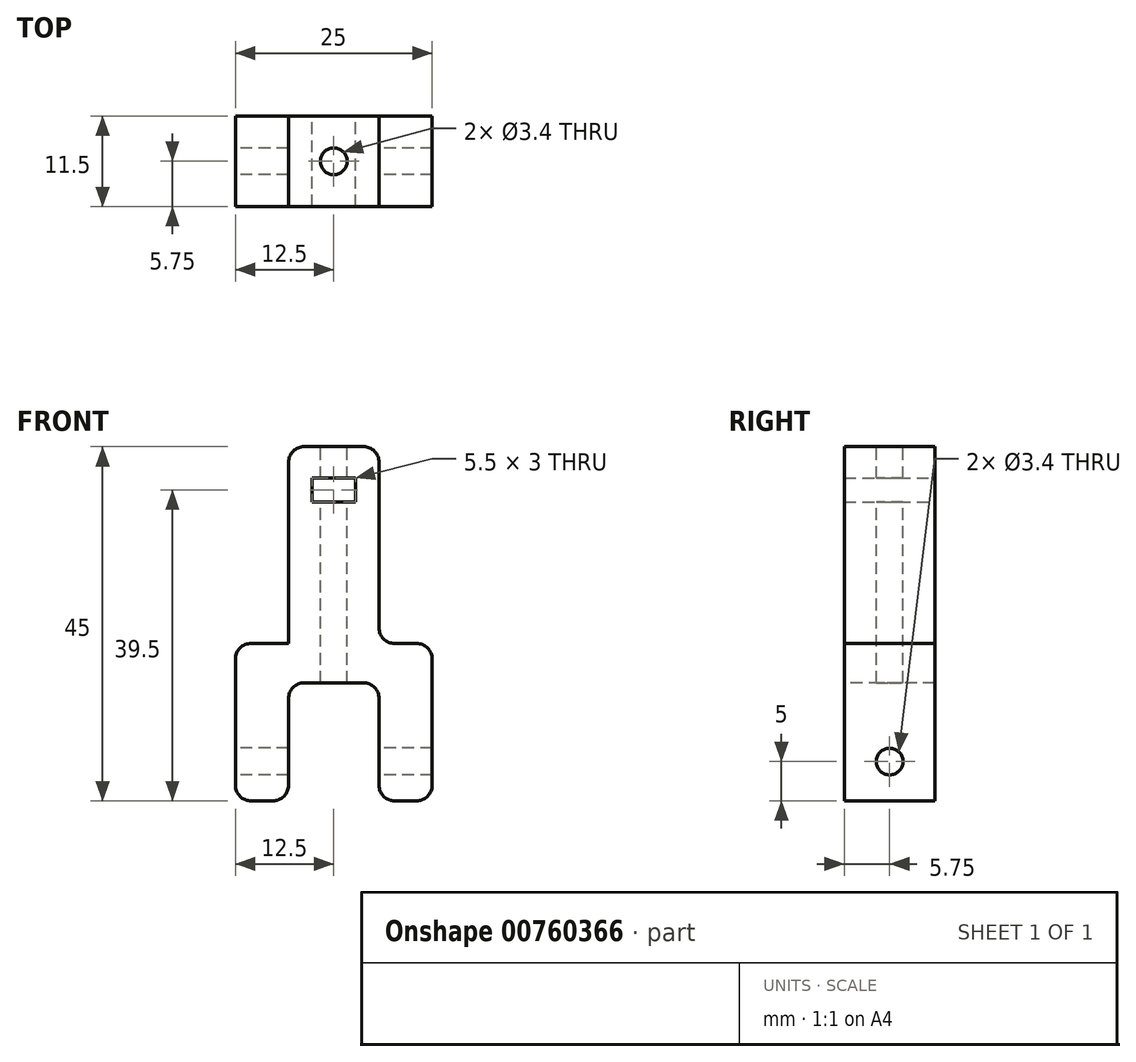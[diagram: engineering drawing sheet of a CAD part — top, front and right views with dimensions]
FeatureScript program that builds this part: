
annotation { "Feature Type Name" : "Feature", "Feature Type Description" : "" }
export const myFeature = defineFeature(function(context is Context, id is Id, definition is map)
    precondition{}
    {
        {
            var Q0;
            Q0=qCreatedBy(makeId("Top.planeOp"),FACE);
            var sketch = newSketch(context, id + "F0", { "sketchPlane" : qUnion([Q0])});
            skLineSegment(sketch, "E0.bottom", {"start": v(5.75, 5.75) * mm, "end": v(-5.75, 5.75) * mm});
            skLineSegment(sketch, "E0.top", {"start": v(5.75, -5.75) * mm, "end": v(-5.75, -5.75) * mm});
            skLineSegment(sketch, "E0.left", {"start": v(5.75, 5.75) * mm, "end": v(5.75, -5.75) * mm});
            skLineSegment(sketch, "E0.right", {"start": v(-5.75, 5.75) * mm, "end": v(-5.75, -5.75) * mm});
            skPoint(sketch, "E0.middle", {"position": v(0, 0) * mm});
            skLineSegment(sketch, "E1.bottom", {"start": v(12.5, 5.75) * mm, "end": v(-12.5, 5.75) * mm});
            skLineSegment(sketch, "E1.top", {"start": v(12.5, -5.75) * mm, "end": v(-12.5, -5.75) * mm});
            skLineSegment(sketch, "E1.left", {"start": v(12.5, 5.75) * mm, "end": v(12.5, -5.75) * mm});
            skLineSegment(sketch, "E1.right", {"start": v(-12.5, 5.75) * mm, "end": v(-12.5, -5.75) * mm});
            skSolve(sketch);
        }
        {
            var Q0;
            {var subQ0=sQuery(id+"F0.wireOp",EDGE,"E0.right");Q0=makeQuery(id+"F0.imprint","IMPRINT",FACE,{"disambiguationData":[TD([[makeQuery(id+"F0.imprint","IMPRINT",EDGE,{"derivedFrom":subQ0}),-1.0]])]});}
            var Q1;
            {var subQ0=sQuery(id+"F0.wireOp",EDGE,"E0.left");Q1=makeQuery(id+"F0.imprint","IMPRINT",FACE,{"disambiguationData":[TD([[makeQuery(id+"F0.imprint","IMPRINT",EDGE,{"derivedFrom":subQ0}),1.0]])]});}
            var Q2;
            {var subQ0=sQuery(id+"F0.wireOp",EDGE,"E0.left");Q2=makeQuery(id+"F0.imprint","IMPRINT",FACE,{"disambiguationData":[TD([[makeQuery(id+"F0.imprint","IMPRINT",EDGE,{"derivedFrom":subQ0}),-1.0]])]});}
            extrude(context, id + "F1", {"entities" : qUnion([Q0, Q1, Q2]), "oppositeDirection" : true, "depth" : 5 * mm});
        }
        {
            var Q0;
            {var subQ0=sQuery(id+"F0.wireOp",EDGE,"E0.left");Q0=makeQuery(id+"F0.imprint","IMPRINT",FACE,{"disambiguationData":[TD([[makeQuery(id+"F0.imprint","IMPRINT",EDGE,{"derivedFrom":subQ0}),1.0]])]});}
            var Q1;
            {var subQ0=sQuery(id+"F0.wireOp",EDGE,"E0.right");Q1=makeQuery(id+"F0.imprint","IMPRINT",FACE,{"disambiguationData":[TD([[makeQuery(id+"F0.imprint","IMPRINT",EDGE,{"derivedFrom":subQ0}),-1.0]])]});}
            extrude(context, id + "F2", {"entities" : qUnion([Q0, Q1]), "operationType" : NewBodyOperationType.ADD, "oppositeDirection" : true, "depth" : 20 * mm});
        }
        {
            var Q0;
            {var subQ0=sQuery(id+"F0.wireOp",EDGE,"E0.left");Q0=makeQuery(id+"F0.imprint","IMPRINT",FACE,{"disambiguationData":[TD([[makeQuery(id+"F0.imprint","IMPRINT",EDGE,{"derivedFrom":subQ0}),-1.0]])]});}
            extrude(context, id + "F3", {"entities" : qUnion([Q0]), "operationType" : NewBodyOperationType.ADD, "depth" : 25 * mm});
        }
        {
            var Q0;
            {var subQ0=sQuery(id+"F0.wireOp",EDGE,"E1.right");Q0=makeQuery(id+"F2.boolean.opBoolean","MERGE",FACE,{"derivedFrom":[makeQuery(id+"F1.opExtrude","SWEPT_FACE",FACE,{"disambiguationData":[OSD([subQ0])]}),makeQuery(id+"F2.opExtrude","SWEPT_FACE",FACE,{"disambiguationData":[OSD([subQ0])]})]});}
            var sketch = newSketch(context, id + "F4", { "sketchPlane" : qUnion([Q0])});
            skCircle(sketch, "E2", {"center": v(0, -15) * mm, "radius": 1.7 * mm});
            skSolve(sketch);
        }
        {
            var Q0;
            Q0=qSketchRegion(id+"F4",true);
            extrude(context, id + "F5", {"entities" : qUnion([Q0]), "operationType" : NewBodyOperationType.REMOVE, "endBound" : BoundingType.THROUGH_ALL, "oppositeDirection" : true, "depth" : 25 * mm});
        }
        {
            var Q0;
            {var subQ0=sQuery(id+"F0.wireOp",EDGE,"E1.bottom");Q0=makeQuery(id+"F3.boolean.opBoolean","MERGE",FACE,{"derivedFrom":[makeQuery(id+"F2.boolean.opBoolean","MERGE",FACE,{"derivedFrom":[makeQuery(id+"F1.opExtrude","SWEPT_FACE",FACE,{"disambiguationData":[OSD([subQ0])]}),makeQuery(id+"F2.opExtrude","SWEPT_FACE",FACE,{"disambiguationData":[OSD([subQ0]),TDD([makeQuery(id+"F0.imprint","IMPRINT",EDGE,{"disambiguationData":[TD([[makeQuery(id+"F0.imprint","INTERSECT",VERTEX,{"derivedFrom":[sQuery(id+"F0.wireOp",EDGE,"E0.left"),subQ0]}),1.0]])],"derivedFrom":subQ0})])]}),makeQuery(id+"F2.opExtrude","SWEPT_FACE",FACE,{"disambiguationData":[OSD([subQ0]),TDD([makeQuery(id+"F0.imprint","IMPRINT",EDGE,{"disambiguationData":[TD([[makeQuery(id+"F0.imprint","INTERSECT",VERTEX,{"derivedFrom":[sQuery(id+"F0.wireOp",EDGE,"E0.right"),subQ0]}),-1.0]])],"derivedFrom":subQ0})])]})]}),makeQuery(id+"F3.opExtrude","SWEPT_FACE",FACE,{"disambiguationData":[OSD([subQ0])]})]});}
            var sketch = newSketch(context, id + "F6", { "sketchPlane" : qUnion([Q0])});
            skLineSegment(sketch, "E3.bottom", {"start": v(2.75, 21) * mm, "end": v(-2.75, 21) * mm});
            skLineSegment(sketch, "E3.top", {"start": v(2.75, 18) * mm, "end": v(-2.75, 18) * mm});
            skLineSegment(sketch, "E3.left", {"start": v(2.75, 21) * mm, "end": v(2.75, 18) * mm});
            skLineSegment(sketch, "E3.right", {"start": v(-2.75, 21) * mm, "end": v(-2.75, 18) * mm});
            skPoint(sketch, "E3.middle", {"position": v(0, 19.5) * mm});
            skSolve(sketch);
        }
        {
            var Q0;
            Q0=makeQuery(id+"F6.imprint","IMPRINT",FACE,{"disambiguationData":[TD([[makeQuery(id+"F6.imprint","IMPRINT",EDGE,{"derivedFrom":sQuery(id+"F6.wireOp",EDGE,"E3.bottom")}),1.0]])]});
            extrude(context, id + "F7", {"entities" : qUnion([Q0]), "operationType" : NewBodyOperationType.REMOVE, "endBound" : BoundingType.THROUGH_ALL, "oppositeDirection" : true, "depth" : 25 * mm});
        }
        {
            var Q0;
            Q0=makeQuery(id+"F3.opExtrude","CAP_FACE",FACE,{"disambiguationData":[OSD([sQuery(id+"F0.wireOp",EDGE,"E0.left"),sQuery(id+"F0.wireOp",EDGE,"E0.right"),sQuery(id+"F0.wireOp",EDGE,"E1.bottom"),sQuery(id+"F0.wireOp",EDGE,"E1.top")])],"isStart":false});
            var sketch = newSketch(context, id + "F8", { "sketchPlane" : qUnion([Q0])});
            skCircle(sketch, "E4", {"center": v(0, 0) * mm, "radius": 1.7 * mm});
            skSolve(sketch);
        }
        {
            var Q0;
            Q0=qSketchRegion(id+"F8",true);
            extrude(context, id + "F9", {"entities" : qUnion([Q0]), "operationType" : NewBodyOperationType.REMOVE, "endBound" : BoundingType.THROUGH_ALL, "oppositeDirection" : true, "depth" : 25 * mm});
        }
        {
            var Q0;
            Q0=makeQuery(id+"F2.opExtrude","CAP_EDGE",EDGE,{"disambiguationData":[OSD([sQuery(id+"F0.wireOp",EDGE,"E0.right")])],"isStart":false});
            var Q1;
            Q1=makeQuery(id+"F2.opExtrude","CAP_EDGE",EDGE,{"disambiguationData":[OSD([sQuery(id+"F0.wireOp",EDGE,"E1.right")])],"isStart":false});
            var Q2;
            Q2=makeQuery(id+"F2.boolean.opBoolean","INTERSECT",EDGE,{"derivedFrom":[makeQuery(id+"F1.opExtrude","CAP_FACE",FACE,{"disambiguationData":[OSD([sQuery(id+"F0.wireOp",EDGE,"E1.bottom"),sQuery(id+"F0.wireOp",EDGE,"E1.top"),sQuery(id+"F0.wireOp",EDGE,"E1.left"),sQuery(id+"F0.wireOp",EDGE,"E1.right")])],"isStart":false}),makeQuery(id+"F2.opExtrude","SWEPT_FACE",FACE,{"disambiguationData":[OSD([sQuery(id+"F0.wireOp",EDGE,"E0.right")])]})]});
            var Q3;
            Q3=makeQuery(id+"F2.boolean.opBoolean","INTERSECT",EDGE,{"derivedFrom":[makeQuery(id+"F1.opExtrude","CAP_FACE",FACE,{"disambiguationData":[OSD([sQuery(id+"F0.wireOp",EDGE,"E1.bottom"),sQuery(id+"F0.wireOp",EDGE,"E1.top"),sQuery(id+"F0.wireOp",EDGE,"E1.left"),sQuery(id+"F0.wireOp",EDGE,"E1.right")])],"isStart":false}),makeQuery(id+"F2.opExtrude","SWEPT_FACE",FACE,{"disambiguationData":[OSD([sQuery(id+"F0.wireOp",EDGE,"E0.left")])]})]});
            var Q4;
            Q4=makeQuery(id+"F2.opExtrude","CAP_EDGE",EDGE,{"disambiguationData":[OSD([sQuery(id+"F0.wireOp",EDGE,"E0.left")])],"isStart":false});
            var Q5;
            Q5=makeQuery(id+"F2.opExtrude","CAP_EDGE",EDGE,{"disambiguationData":[OSD([sQuery(id+"F0.wireOp",EDGE,"E1.left")])],"isStart":false});
            var Q6;
            Q6=makeQuery(id+"F1.opExtrude","CAP_EDGE",EDGE,{"disambiguationData":[OSD([sQuery(id+"F0.wireOp",EDGE,"E1.left")])],"isStart":true});
            var Q7;
            Q7=makeQuery(id+"F1.opExtrude","CAP_EDGE",EDGE,{"disambiguationData":[OSD([sQuery(id+"F0.wireOp",EDGE,"E1.right")])],"isStart":true});
            var Q8;
            Q8=makeQuery(id+"F3.opExtrude","CAP_EDGE",EDGE,{"disambiguationData":[OSD([sQuery(id+"F0.wireOp",EDGE,"E0.right")])],"isStart":true});
            var Q9;
            Q9=makeQuery(id+"F3.opExtrude","CAP_EDGE",EDGE,{"disambiguationData":[OSD([sQuery(id+"F0.wireOp",EDGE,"E0.right")])],"isStart":false});
            var Q10;
            Q10=makeQuery(id+"F3.opExtrude","CAP_EDGE",EDGE,{"disambiguationData":[OSD([sQuery(id+"F0.wireOp",EDGE,"E0.left")])],"isStart":false});
            var Q11;
            Q11=makeQuery(id+"F3.opExtrude","CAP_EDGE",EDGE,{"disambiguationData":[OSD([sQuery(id+"F0.wireOp",EDGE,"E0.left")])],"isStart":true});
            fillet(context, id + "F10", {"entities" : qUnion([Q0, Q1, Q2, Q3, Q4, Q5, Q6, Q7, Q8, Q9, Q10, Q11]), "radius" : 2 * mm, "tangentPropagation" : true, "allowEdgeOverflow" : false});
        }
    });
